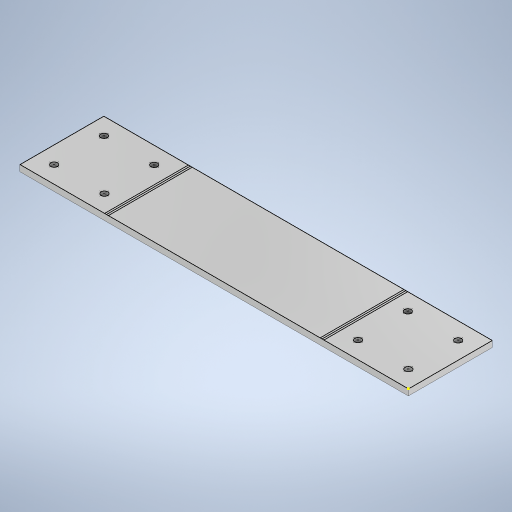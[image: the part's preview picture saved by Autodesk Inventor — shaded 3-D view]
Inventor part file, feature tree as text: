
AUTODESK INVENTOR PART (.ipt)
format: ipt  version: 2024.2 (Build 282272000, 272)  size: 240,640 bytes
history: native  units: in
note: dims shown in document units (in); Inventor stores cm internally (conversion verified against a paired STEP export)
features: sketch x1, extrude x1
ambient origin geometry x8: Origin, YZ Plane, XZ Plane, XY Plane, X Axis, Y Axis, Z Axis, Center Point
bodies: Solid1 (feature_tree)
feature tree (2):
  sketch  "Sketch1"  dims[d0=0.0591in d1=0.0in]
  extrude  "Extrusion1"  [1 undecoded]
note: 1 required parameter value undecoded (feature->parameter linkage not recoverable at this tier; creation-order binding heuristic only, values carry confidence <= 0.55)
